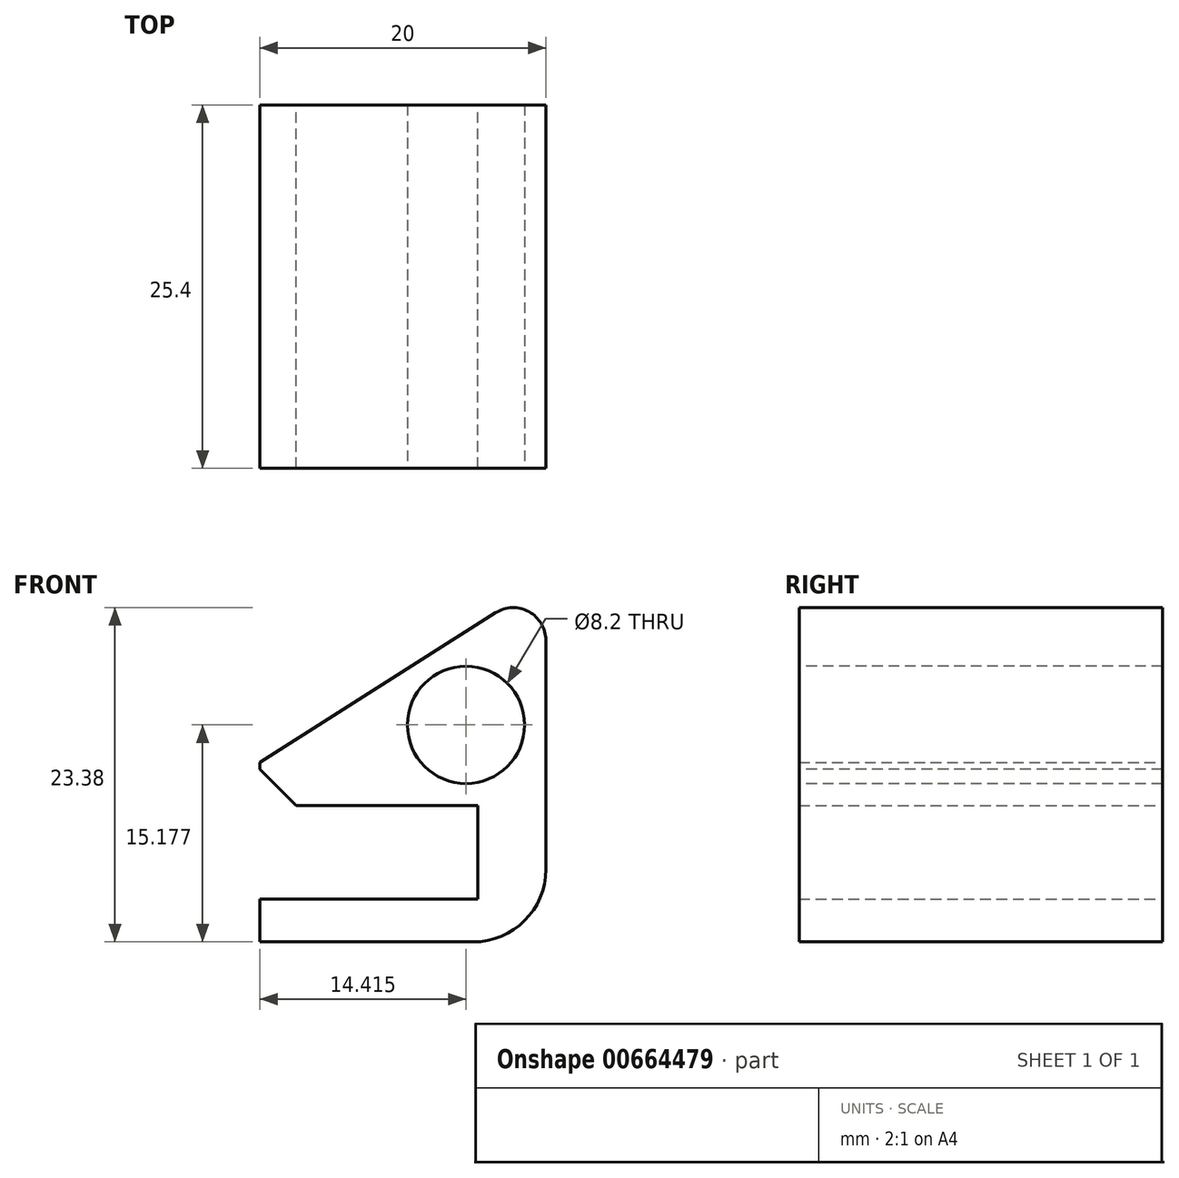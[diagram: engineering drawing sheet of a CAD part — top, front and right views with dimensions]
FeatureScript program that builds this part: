
annotation { "Feature Type Name" : "Feature", "Feature Type Description" : "" }
export const myFeature = defineFeature(function(context is Context, id is Id, definition is map)
    precondition{}
    {
        {
            var Q0;
            Q0=qCreatedBy(makeId("Front.planeOp"),FACE);
            var sketch = newSketch(context, id + "F0", { "sketchPlane" : qUnion([Q0])});
            skLineSegment(sketch, "E0", {"start": v(0, 0) * mm, "end": v(0, -6.55) * mm});
            skLineSegment(sketch, "E1", {"start": v(0, -6.55) * mm, "end": v(-15.24, -6.55) * mm});
            skLineSegment(sketch, "E2", {"start": v(-15.24, -6.55) * mm, "end": v(0, -6.55) * mm});
            skLineSegment(sketch, "E3", {"start": v(0, 0) * mm, "end": v(-15.24, 0) * mm});
            skLineSegment(sketch, "E4", {"start": v(-15.24, -6.55) * mm, "end": v(-15.24, -9.55) * mm});
            skLineSegment(sketch, "E5", {"start": v(-15.24, -9.55) * mm, "end": v(-15.24, -6.55) * mm});
            skLineSegment(sketch, "E6", {"start": v(-15.24, 0) * mm, "end": v(-15.24, 3) * mm});
            skLineSegment(sketch, "E7", {"start": v(-15.24, 3) * mm, "end": v(4.76, 3) * mm});
            skLineSegment(sketch, "E8", {"start": v(-15.24, -9.55) * mm, "end": v(4.76, -9.55) * mm});
            skLineSegment(sketch, "E9", {"start": v(4.76, -9.55) * mm, "end": v(4.76, 3) * mm});
            skLineSegment(sketch, "E10", {"start": v(4.76, 3) * mm, "end": v(4.76, 15.7) * mm});
            skLineSegment(sketch, "E11", {"start": v(-15.24, 3) * mm, "end": v(4.76, 15.7) * mm});
            skSolve(sketch);
        }
        {
            var Q0;
            Q0=makeQuery(id+"F0.imprint","IMPRINT",FACE,{"disambiguationData":[TD([[makeQuery(id+"F0.imprint","IMPRINT",EDGE,{"derivedFrom":sQuery(id+"F0.wireOp",EDGE,"E0")}),1.0]])]});
            extrude(context, id + "F1", {"entities" : qUnion([Q0]), "depth" : 25.4 * mm, "offsetDistance" : 25.4 * mm});
        }
        {
            var Q0;
            Q0=makeQuery(id+"F0.imprint","IMPRINT",FACE,{"disambiguationData":[TD([[makeQuery(id+"F0.imprint","IMPRINT",EDGE,{"derivedFrom":sQuery(id+"F0.wireOp",EDGE,"E7")}),1.0]])]});
            extrude(context, id + "F2", {"entities" : qUnion([Q0]), "operationType" : NewBodyOperationType.ADD, "depth" : 25.4 * mm, "offsetDistance" : 25.4 * mm});
        }
        {
            var Q0;
            Q0=makeQuery(id+"F1.opExtrude","SWEPT_EDGE",EDGE,{"disambiguationData":[OSD([sQuery(id+"F0.wireOp",EDGE,"E8"),sQuery(id+"F0.wireOp",EDGE,"E9")])]});
            fillet(context, id + "F3", {"entities" : qUnion([Q0]), "radius" : 5.08 * mm, "tangentPropagation" : true, "allowEdgeOverflow" : false});
        }
        {
            var Q0;
            Q0=makeQuery(id+"F2.opExtrude","SWEPT_EDGE",EDGE,{"disambiguationData":[OSD([sQuery(id+"F0.wireOp",EDGE,"E10"),sQuery(id+"F0.wireOp",EDGE,"E11")])]});
            fillet(context, id + "F4", {"entities" : qUnion([Q0]), "radius" : 2.3 * mm, "tangentPropagation" : true, "allowEdgeOverflow" : false});
        }
        {
            var Q0;
            Q0=makeQuery(id+"F1.opExtrude","SWEPT_EDGE",EDGE,{"disambiguationData":[OSD([sQuery(id+"F0.wireOp",EDGE,"E3"),sQuery(id+"F0.wireOp",EDGE,"E6")])]});
            var Q1;
            Q1=makeQuery(id+"F1.opExtrude","SWEPT_EDGE",EDGE,{"disambiguationData":[OSD([sQuery(id+"F0.wireOp",EDGE,"E2"),sQuery(id+"F0.wireOp",EDGE,"E5")])]});
            chamfer(context, id + "F5", {"entities" : qUnion([Q0, Q1]), "width" : 2.54 * mm, "tangentPropagation" : true});
        }
        {
            var Q0;
            Q0=qCreatedBy(makeId("Front.planeOp"),FACE);
            var sketch = newSketch(context, id + "F6", { "sketchPlane" : qUnion([Q0])});
            skCircle(sketch, "E12", {"center": v(-0.82, 5.63) * mm, "radius": 4.1 * mm});
            skSolve(sketch);
        }
        {
            var Q0;
            Q0 = qSketchRegion(id + "F6", true);
            extrude(context, id + "F7", {"entities" : qUnion([Q0]), "operationType" : NewBodyOperationType.REMOVE, "oppositeDirection" : true, "depth" : 25.4 * mm, "offsetDistance" : 25.4 * mm, "hasSecondDirection" : true, "secondDirectionOppositeDirection" : false, "secondDirectionDepth" : 254 * mm});
        }
    });
